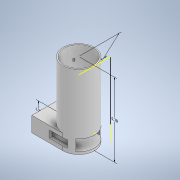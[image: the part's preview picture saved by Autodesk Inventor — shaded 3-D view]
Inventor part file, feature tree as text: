
AUTODESK INVENTOR PART (.ipt)
format: ipt  version: 2021 (Build 250183000, 183)  size: 206,336 bytes
history: native  units: in
note: dims shown in document units (in); Inventor stores cm internally (conversion verified against a paired STEP export)
features: sketch x13, extrude x9, other x4, plane x1
ambient origin geometry x8: Origin, YZ Plane, XZ Plane, XY Plane, X Axis, Y Axis, Z Axis, Center Point
bodies: Solid1 (feature_tree)
feature tree (27):
  other  "Annotations"
  sketch  "Sketch1"  dims[d0=2.7in d1=5.0in d2=0.0in]
  extrude  "BaseCup"  Depth=5.0in TaperAngle=0.0deg
  extrude  "Extrusion2"  Depth=5.3125in TaperAngle=0.0deg
  extrude  "Extrusion3"  Depth=1.3in TaperAngle=0.0deg
  plane  "Work Plane1"
  sketch  "Sketch5"  dims[d12=9.05in d13=0.0in d14=2.65in d15=0.0in]
  extrude  "Extrusion4"  Depth=2.25in
  extrude  "Extrusion5"  Depth=2.65in TaperAngle=0.0deg
  extrude  "Extrusion6"  Depth=1.0in
  extrude  "Extrusion7"  Depth=0.6in
  sketch  "Sketch12"  dims[d29=0.1in]
  sketch  "Sketch13"  dims[d30=0.2in]
  extrude  "Extrusion8"  Depth=1.0in
  extrude  "Extrusion9"  Depth=0.2in
  sketch  "Sketch2"  dims[d3=2.5in d4=5.3125in d5=0.0in]
  sketch  "Sketch3"  dims[d6=2.7in d7=1.3in d8=0.0in]
  sketch  "Sketch4"  dims[d10=0.95in d11=2.25in]
  sketch  "Sketch6"  dims[d17=3.9125in d18=0.0in d19=1.0in]
  sketch  "Sketch9"  dims[d20=1.5in d21=0.6in]
  sketch  "Sketch10"  dims[d22=3.4in d23=0.0in d26=1.0in]
  sketch  "Sketch11"  dims[d27=0.6in d28=0.2in]
  sketch  "Sketch14"  dims[d31=0.1in]
  sketch  "Sketch15"  dims[d32=0.6in d33=0.2in d34=0.1in d35=3.9in d36=0.0in d37=0.7in d38=0.9in d39=3.9in d40=0.0in d16=6.3in d24=0.306in d25=5.6588in d9=1.3in]
  other  "Linear Dimension 1"
  other  "Linear Dimension 2"
  other  "Linear Dimension 3"
